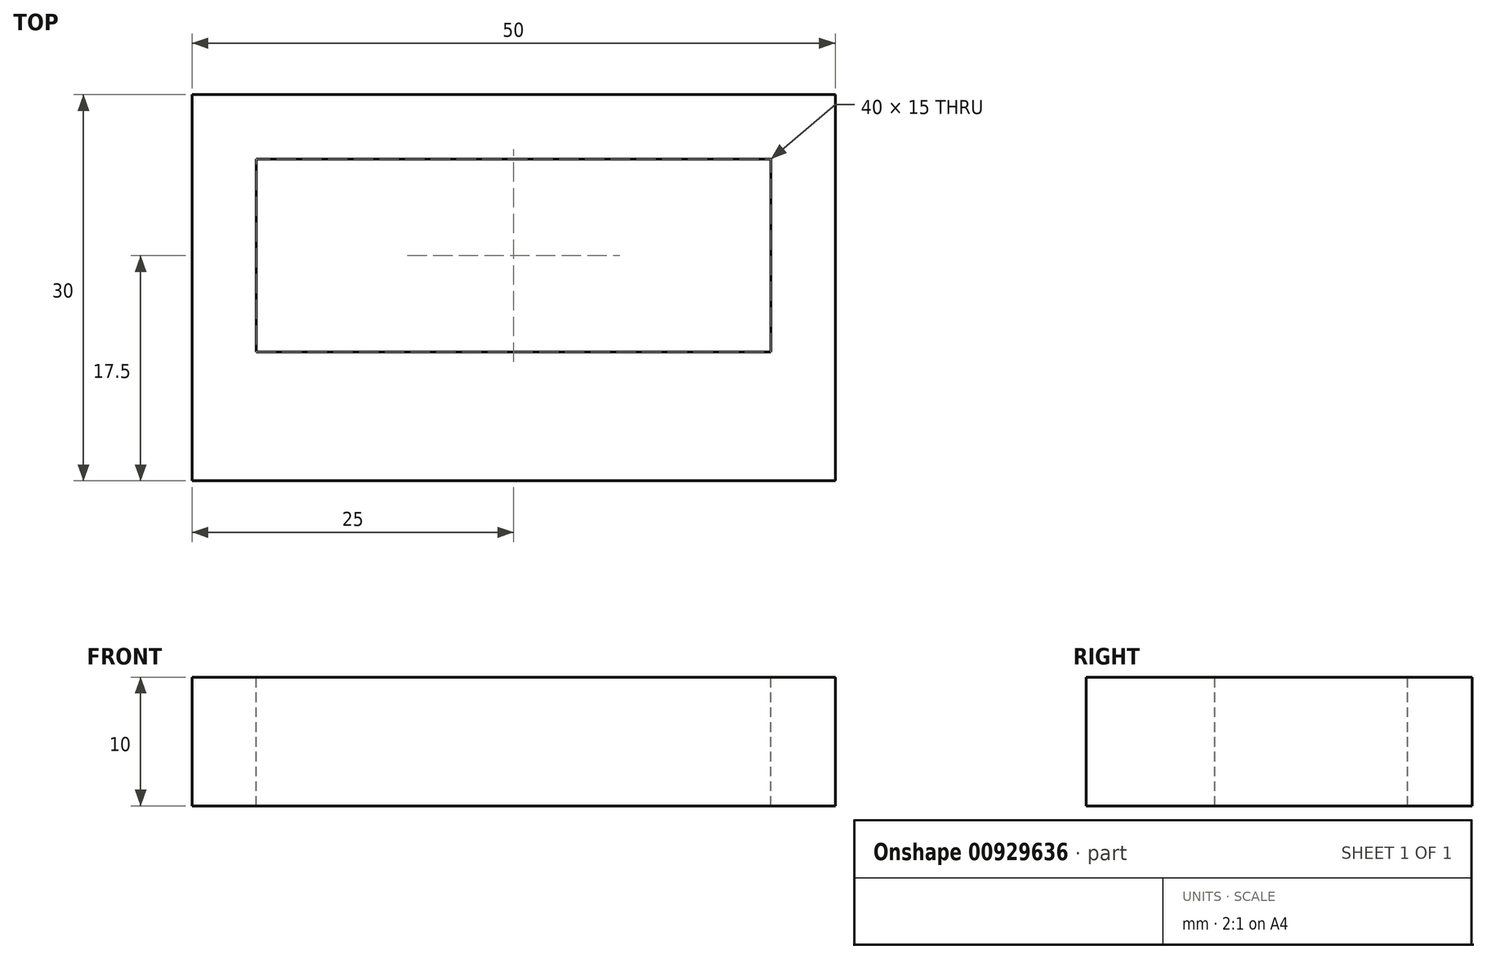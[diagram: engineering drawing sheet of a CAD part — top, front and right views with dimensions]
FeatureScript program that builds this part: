
annotation { "Feature Type Name" : "Feature", "Feature Type Description" : "" }
export const myFeature = defineFeature(function(context is Context, id is Id, definition is map)
    precondition{}
    {
        {
            var Q0;
            Q0=qCreatedBy(makeId("Top.planeOp"),FACE);
            var sketch = newSketch(context, id + "F0", { "sketchPlane" : qUnion([Q0])});
            skLineSegment(sketch, "E0.bottom", {"start": v(0, 0) * mm, "end": v(50, 0) * mm});
            skLineSegment(sketch, "E0.top", {"start": v(0, 30) * mm, "end": v(50, 30) * mm});
            skLineSegment(sketch, "E0.left", {"start": v(0, 0) * mm, "end": v(0, 30) * mm});
            skLineSegment(sketch, "E0.right", {"start": v(50, 0) * mm, "end": v(50, 30) * mm});
            skSolve(sketch);
        }
        {
            var Q0;
            Q0 = qSketchRegion(id + "F0", true);
            extrude(context, id + "F1", {"entities" : qUnion([Q0]), "depth" : 10 * mm, "offsetDistance" : 25 * mm});
        }
        {
            var Q0;
            Q0=makeQuery(id+"F1.opExtrude","CAP_FACE",FACE,{"disambiguationData":[OSD([sQuery(id+"F0.wireOp",EDGE,"E0.bottom"),sQuery(id+"F0.wireOp",EDGE,"E0.top"),sQuery(id+"F0.wireOp",EDGE,"E0.left"),sQuery(id+"F0.wireOp",EDGE,"E0.right")])],"isStart":false});
            var sketch = newSketch(context, id + "F2", { "sketchPlane" : qUnion([Q0])});
            skLineSegment(sketch, "E1.0", {"start": v(45, 0) * mm, "end": v(45, 25) * mm});
            skLineSegment(sketch, "E1.1", {"start": v(5, 25) * mm, "end": v(45, 25) * mm});
            skLineSegment(sketch, "E1.2", {"start": v(5, 0) * mm, "end": v(5, 25) * mm});
            skLineSegment(sketch, "E2", {"start": v(5, 10) * mm, "end": v(45, 10) * mm});
            skPoint(sketch, "E2.endSnap0", {"position": v(45, 12.5) * mm});
            skSolve(sketch);
        }
        {
            var Q0;
            {var subQ0=sQuery(id+"F2.wireOp",EDGE,"E1.1");Q0=makeQuery(id+"F2.imprint","IMPRINT",FACE,{"disambiguationData":[TD([[makeQuery(id+"F2.imprint","IMPRINT",EDGE,{"derivedFrom":subQ0}),-1.0]])]});}
            extrude(context, id + "F3", {"entities" : qUnion([Q0]), "operationType" : NewBodyOperationType.REMOVE, "endBound" : BoundingType.UP_TO_NEXT, "oppositeDirection" : true, "depth" : 25 * mm, "offsetDistance" : 25 * mm});
        }
    });
